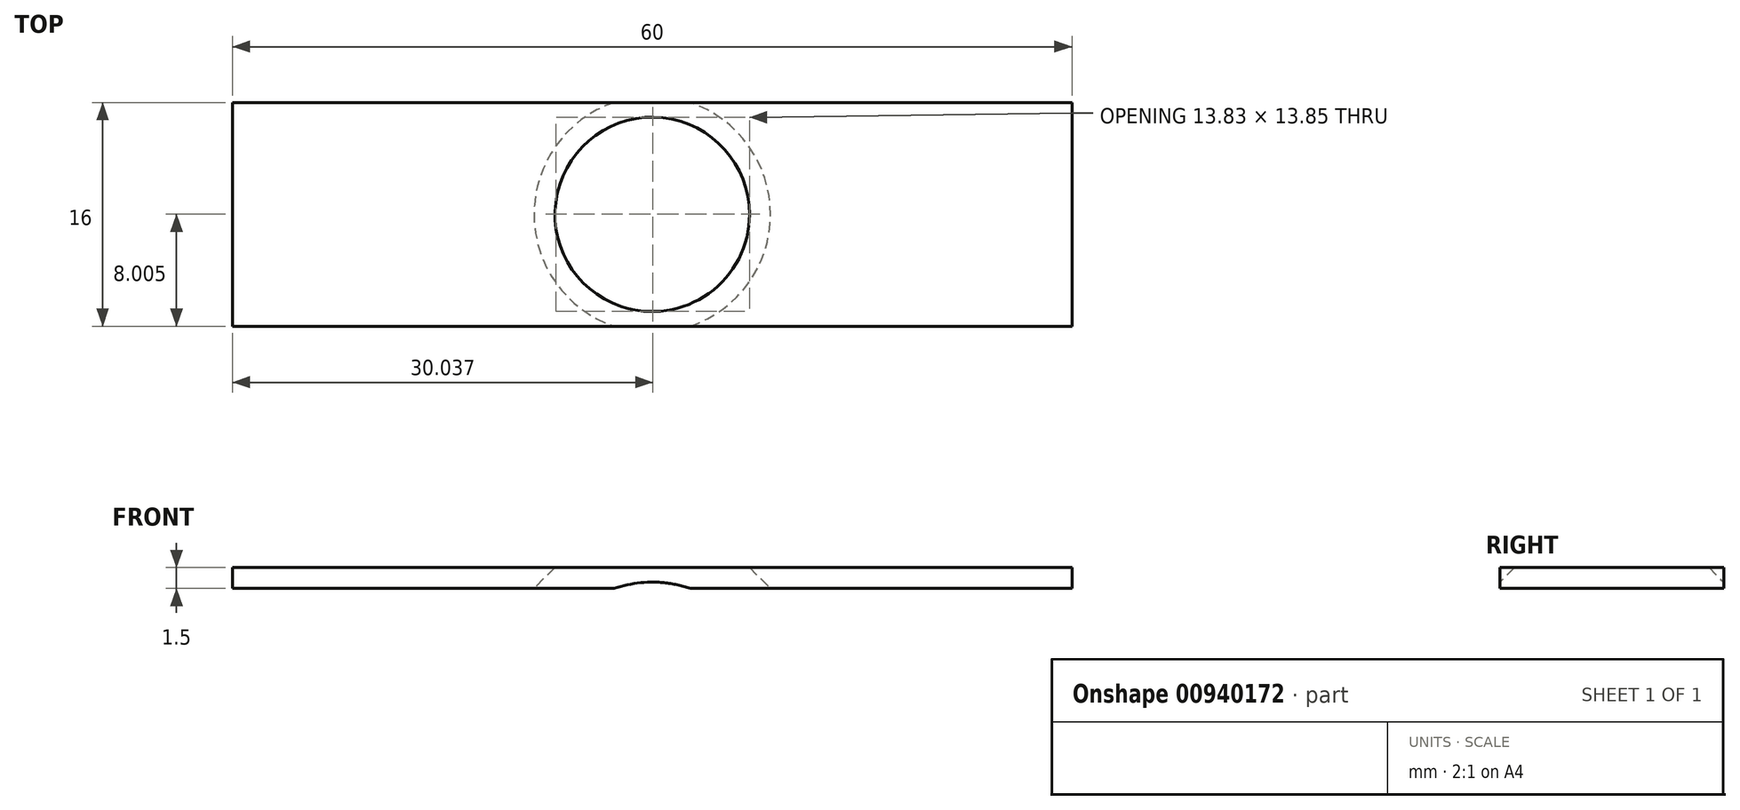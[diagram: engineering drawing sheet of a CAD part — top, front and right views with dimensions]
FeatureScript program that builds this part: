
annotation { "Feature Type Name" : "Feature", "Feature Type Description" : "" }
export const myFeature = defineFeature(function(context is Context, id is Id, definition is map)
    precondition{}
    {
        {
            var Q0;
            Q0=qCreatedBy(makeId("Top.planeOp"),FACE);
            var sketch = newSketch(context, id + "F0", { "sketchPlane" : qUnion([Q0])});
            skCircle(sketch, "E0", {"center": v(0, 0) * mm, "radius": 6.95 * mm});
            skLineSegment(sketch, "E1.bottom", {"start": v(-30, -8) * mm, "end": v(30, -8) * mm});
            skLineSegment(sketch, "E1.top", {"start": v(-30, 8) * mm, "end": v(30, 8) * mm});
            skLineSegment(sketch, "E1.left", {"start": v(-30, -8) * mm, "end": v(-30, 8) * mm});
            skLineSegment(sketch, "E1.right", {"start": v(30, -8) * mm, "end": v(30, 8) * mm});
            skSolve(sketch);
        }
        {
            var Q0;
            Q0 = qSketchRegion(id + "F0", true);
            extrude(context, id + "F1", {"entities" : qUnion([Q0]), "depth" : 1.5 * mm, "offsetDistance" : 25 * mm});
        }
        {
            var Q0;
            Q0=makeQuery(id+"F1.opExtrude","CAP_EDGE",EDGE,{"disambiguationData":[OSD([sQuery(id+"F0.wireOp",EDGE,"E0")])],"isStart":true});
            chamfer(context, id + "F2", {"entities" : qUnion([Q0]), "width" : 1.5 * mm, "tangentPropagation" : true});
        }
    });
